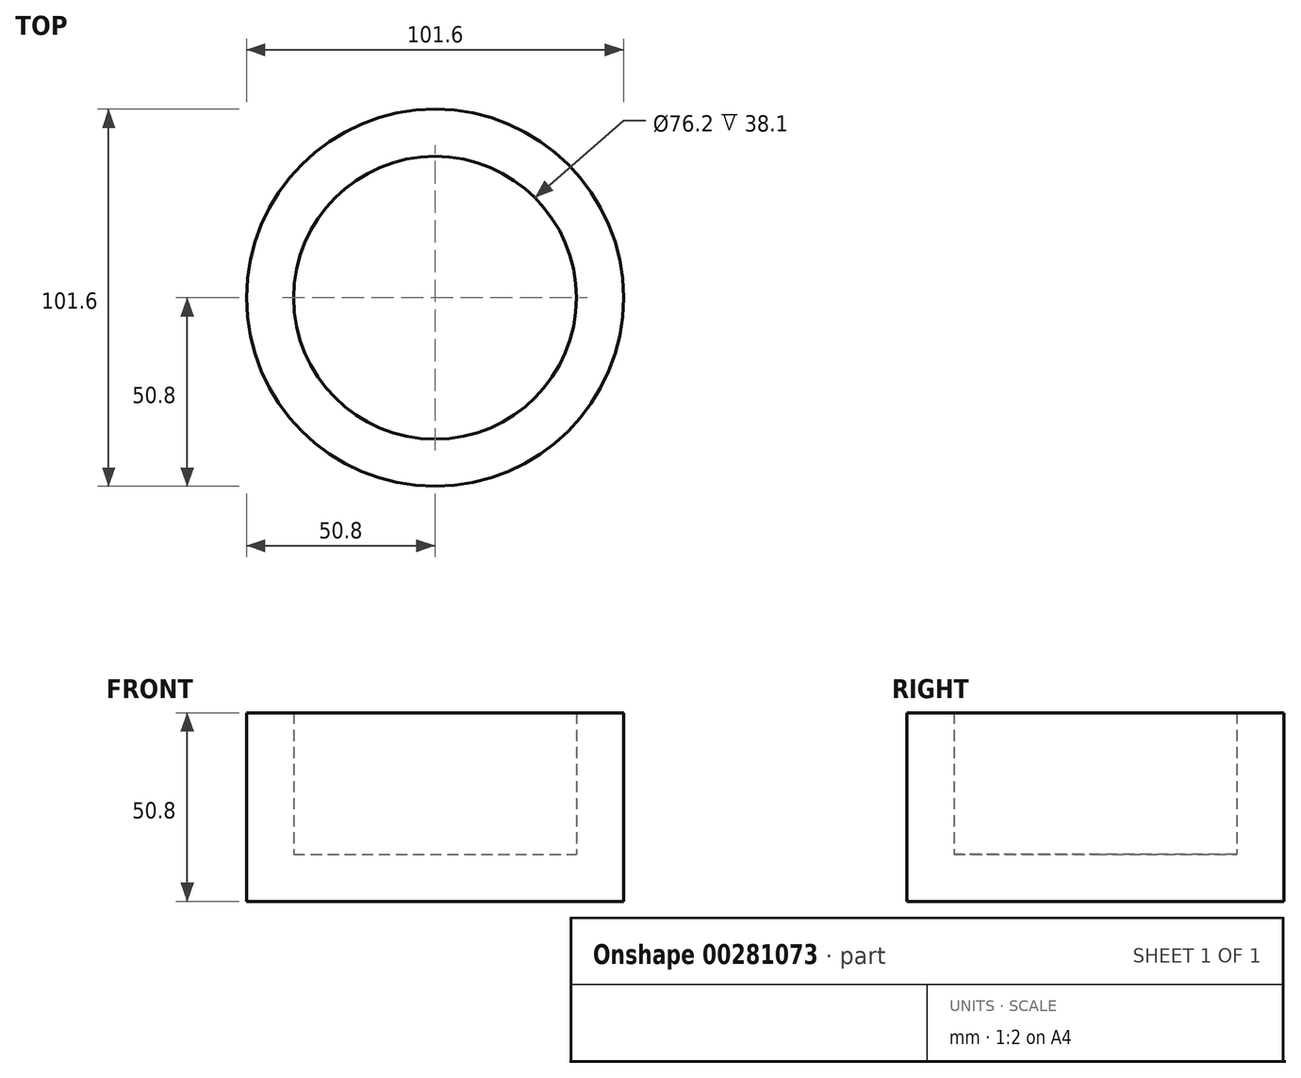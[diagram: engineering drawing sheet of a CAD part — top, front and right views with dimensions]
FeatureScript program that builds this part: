
annotation { "Feature Type Name" : "Feature", "Feature Type Description" : "" }
export const myFeature = defineFeature(function(context is Context, id is Id, definition is map)
    precondition{}
    {
        {
            var Q0;
            Q0=qCreatedBy(makeId("Front.planeOp"),FACE);
            var sketch = newSketch(context, id + "F0", { "sketchPlane" : qUnion([Q0])});
            skLineSegment(sketch, "E0", {"start": v(0, 0) * mm, "end": v(0, 74.1) * mm, "construction": true});
            skLineSegment(sketch, "E1.bottom", {"start": v(0, 0) * mm, "end": v(-50.8, 0) * mm});
            skLineSegment(sketch, "E1.top", {"start": v(0, 50.8) * mm, "end": v(-50.8, 50.8) * mm});
            skLineSegment(sketch, "E1.left", {"start": v(0, 0) * mm, "end": v(0, 50.8) * mm});
            skLineSegment(sketch, "E1.right", {"start": v(-50.8, 0) * mm, "end": v(-50.8, 50.8) * mm});
            skSolve(sketch);
        }
        {
            var Q0;
            Q0=makeQuery(id+"F0.imprint","IMPRINT",FACE,{"disambiguationData":[TD([[makeQuery(id+"F0.imprint","IMPRINT",EDGE,{"derivedFrom":sQuery(id+"F0.wireOp",EDGE,"E1.bottom")}),-1.0]])]});
            var Q1;
            Q1=sQuery(id+"F0.wireOp",EDGE,"E0");
            revolve(context, id + "F1", {"entities" : qUnion([Q0]), "axis" : qUnion([Q1]), "revolveType" : RevolveType.FULL});
        }
        {
            var Q0;
            Q0=makeQuery(id+"F1.opRevolve","SWEPT_FACE",FACE,{"disambiguationData":[OSD([sQuery(id+"F0.wireOp",EDGE,"E1.top")])]});
            shell(context, id + "F2", {"entities" : qUnion([Q0]), "thickness" : 12.7 * mm});
        }
    });
